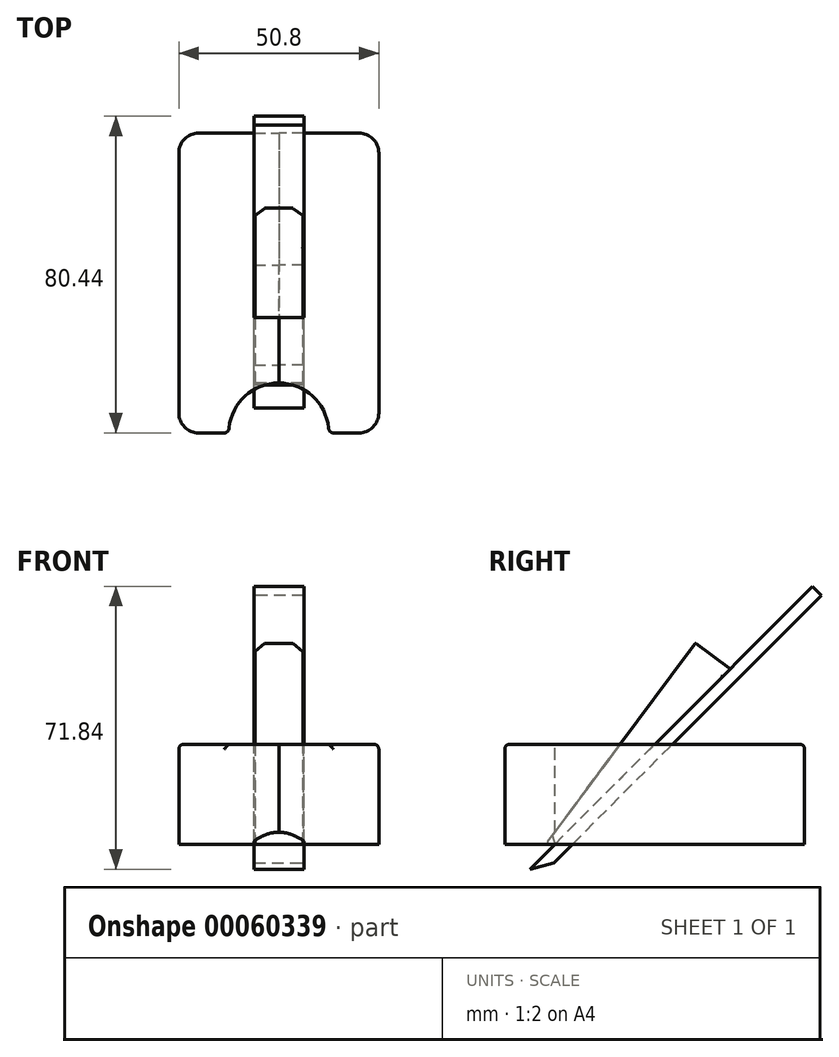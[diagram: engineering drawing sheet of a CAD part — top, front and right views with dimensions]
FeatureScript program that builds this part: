
annotation { "Feature Type Name" : "Feature", "Feature Type Description" : "" }
export const myFeature = defineFeature(function(context is Context, id is Id, definition is map)
    precondition{}
    {
        {
            var Q0;
            Q0=qCreatedBy(makeId("Right.planeOp"),FACE);
            var sketch = newSketch(context, id + "F0", { "sketchPlane" : qUnion([Q0])});
            skLineSegment(sketch, "E0.bottom", {"start": v(38.1, 0) * mm, "end": v(-38.1, 0) * mm});
            skLineSegment(sketch, "E0.top", {"start": v(38.1, 25.4) * mm, "end": v(-38.1, 25.4) * mm});
            skLineSegment(sketch, "E0.left", {"start": v(38.1, 0) * mm, "end": v(38.1, 25.4) * mm});
            skLineSegment(sketch, "E0.right", {"start": v(-38.1, 0) * mm, "end": v(-38.1, 25.4) * mm});
            skSolve(sketch);
        }
        {
            var Q0;
            Q0=qSketchRegion(id+"F0",true);
            extrude(context, id + "F1", {"entities" : qUnion([Q0]), "depth" : 25.4 * mm});
        }
        {
            var Q0;
            Q0=qCreatedBy(makeId("Right.planeOp"),FACE);
            var sketch = newSketch(context, id + "F2", { "sketchPlane" : qUnion([Q0])});
            skLineSegment(sketch, "E1", {"start": v(-29.5, -8.6) * mm, "end": v(42.34, 63.25) * mm});
            skLineSegment(sketch, "E2", {"start": v(40.1, 65.5) * mm, "end": v(42.34, 63.25) * mm});
            skLineSegment(sketch, "E3", {"start": v(-31.75, -6.35) * mm, "end": v(-29.5, -8.6) * mm});
            skLineSegment(sketch, "E4", {"start": v(19.15, 44.55) * mm, "end": v(10.32, 51.1) * mm});
            skLineSegment(sketch, "E5", {"start": v(10.32, 51.1) * mm, "end": v(-26, 2.23) * mm});
            skLineSegment(sketch, "E6", {"start": v(-26, 2.23) * mm, "end": v(-25.4, 0) * mm});
            skLineSegment(sketch, "E7", {"start": v(0, 0) * mm, "end": v(72.47, 0) * mm, "construction": true});
            skLineSegment(sketch, "E8", {"start": v(-25.4, 0) * mm, "end": v(19.15, 44.55) * mm});
            skLineSegment(sketch, "E9", {"start": v(40.1, 65.5) * mm, "end": v(-31.75, -6.35) * mm});
            skSolve(sketch);
        }
        {
            var Q0;
            Q0=qCreatedBy(makeId("Right.planeOp"),FACE);
            var sketch = newSketch(context, id + "F3", { "sketchPlane" : qUnion([Q0])});
            skLineSegment(sketch, "E10", {"start": v(-20.9, 0) * mm, "end": v(4.5, 25.4) * mm});
            skLineSegment(sketch, "E11", {"start": v(-27.66, 0) * mm, "end": v(-20.9, 0) * mm});
            skLineSegment(sketch, "E12", {"start": v(-27.66, 0) * mm, "end": v(-8.78, 25.4) * mm});
            skLineSegment(sketch, "E13", {"start": v(4.5, 25.4) * mm, "end": v(-8.78, 25.4) * mm});
            skSolve(sketch);
        }
        {
            var Q0;
            Q0=qSketchRegion(id+"F3",true);
            extrude(context, id + "F4", {"entities" : qUnion([Q0]), "operationType" : NewBodyOperationType.REMOVE, "depth" : 6.35 * mm});
        }
        {
            var Q0;
            Q0=makeQuery(id+"F1.opExtrude","SWEPT_FACE",FACE,{"disambiguationData":[OSD([sQuery(id+"F0.wireOp",EDGE,"E0.top")])]});
            var sketch = newSketch(context, id + "F5", { "sketchPlane" : qUnion([Q0])});
            skCircle(sketch, "E14", {"center": v(0, -38.1) * mm, "radius": 12.7 * mm});
            skSolve(sketch);
        }
        {
            var Q0;
            {var subQ0=sQuery(id+"F5.wireOp",EDGE,"E14");var subQ1=sQuery(id+"F0.wireOp",EDGE,"E0.right");var subQ2=sQuery(id+"F0.wireOp",EDGE,"E0.top");var subQ3=makeQuery(id+"F9.opPattern","COPY",EDGE,{"derivedFrom":makeQuery(id+"F1.opExtrude","SWEPT_EDGE",EDGE,{"disambiguationData":[OSD([subQ2,subQ1])]}),"instanceName":"1"});var subQ4=makeQuery(id+"F5.imprint","INTERSECT",VERTEX,{"derivedFrom":[subQ3,subQ0]});Q0=makeQuery(id+"F5.imprint","IMPRINT",FACE,{"disambiguationData":[TD([[makeQuery(id+"F5.imprint","IMPRINT",EDGE,{"disambiguationData":[TD([[subQ4,-1.0]])],"derivedFrom":subQ0}),1.0]])]});}
            extrude(context, id + "F6", {"entities" : qUnion([Q0]), "operationType" : NewBodyOperationType.REMOVE, "endBound" : BoundingType.THROUGH_ALL, "oppositeDirection" : true, "depth" : 25.4 * mm});
        }
        {
            var Q0;
            Q0=makeQuery(id+"F1.opExtrude","CAP_EDGE",EDGE,{"disambiguationData":[OSD([sQuery(id+"F0.wireOp",EDGE,"E0.right")])],"isStart":false});
            var Q1;
            Q1=makeQuery(id+"F1.opExtrude","CAP_EDGE",EDGE,{"disambiguationData":[OSD([sQuery(id+"F0.wireOp",EDGE,"E0.left")])],"isStart":false});
            fillet(context, id + "F7", {"entities" : qUnion([Q0, Q1]), "radius" : 5.08 * mm, "tangentPropagation" : true, "allowEdgeOverflow" : false});
        }
        {
            var Q0;
            Q0=makeQuery(id+"F1.opExtrude","CAP_EDGE",EDGE,{"disambiguationData":[OSD([sQuery(id+"F0.wireOp",EDGE,"E0.top")])],"isStart":false});
            var Q1;
            Q1=makeQuery(id+"F6.boolean.opBoolean","COPY",EDGE,{"derivedFrom":makeQuery(id+"F6.opExtrude","CAP_EDGE",EDGE,{"disambiguationData":[OSD([sQuery(id+"F5.wireOp",EDGE,"E14")])],"isStart":true})});
            var Q2;
            Q2=makeQuery(id+"F6.boolean.opBoolean","INTERSECT",EDGE,{"derivedFrom":[makeQuery(id+"F1.opExtrude","SWEPT_FACE",FACE,{"disambiguationData":[OSD([sQuery(id+"F0.wireOp",EDGE,"E0.right")])]}),makeQuery(id+"F6.opExtrude","SWEPT_FACE",FACE,{"disambiguationData":[OSD([sQuery(id+"F5.wireOp",EDGE,"E14")])]})]});
            fillet(context, id + "F8", {"entities" : qUnion([Q0, Q1, Q2]), "radius" : 1.27 * mm, "tangentPropagation" : true, "allowEdgeOverflow" : false});
        }
        {
            var Q0;
            Q0=makeQuery(id+"F1.opExtrude","SWEPT_BODY",BODY,{"disambiguationData":[OSD([sQuery(id+"F0.wireOp",EDGE,"E0.bottom"),sQuery(id+"F0.wireOp",EDGE,"E0.top"),sQuery(id+"F0.wireOp",EDGE,"E0.left"),sQuery(id+"F0.wireOp",EDGE,"E0.right")])]});
            var Q1;
            Q1=qCreatedBy(makeId("Right.planeOp"),FACE);
            mirror(context, id + "F9", {"entities" : qUnion([Q0]), "mirrorPlane" : qUnion([Q1])});
        }
        {
            var Q0;
            Q0=qCreatedBy(makeId("Right.planeOp"),FACE);
            var sketch = newSketch(context, id + "F10", { "sketchPlane" : qUnion([Q0])});
            skLineSegment(sketch, "E15.0", {"start": v(10.32, 51.1) * mm, "end": v(-26, 2.23) * mm});
            skLineSegment(sketch, "E16.0", {"start": v(-25.4, 0) * mm, "end": v(19.15, 44.55) * mm});
            skLineSegment(sketch, "E17.0", {"start": v(-26, 2.23) * mm, "end": v(-25.4, 0) * mm});
            skLineSegment(sketch, "E18.0", {"start": v(19.15, 44.55) * mm, "end": v(10.32, 51.1) * mm});
            skSolve(sketch);
        }
        {
            var Q0;
            Q0=qSketchRegion(id+"F10",true);
            extrude(context, id + "F11", {"entities" : qUnion([Q0]), "endBound" : BoundingType.SYMMETRIC, "depth" : 12.2 * mm});
        }
        {
            var Q0;
            Q0=qCreatedBy(makeId("Right.planeOp"),FACE);
            var sketch = newSketch(context, id + "F12", { "sketchPlane" : qUnion([Q0])});
            skLineSegment(sketch, "E19.0", {"start": v(-31.75, -6.35) * mm, "end": v(-29.5, -8.6) * mm});
            skLineSegment(sketch, "E20.0", {"start": v(-31.75, -6.35) * mm, "end": v(40.1, 65.5) * mm});
            skLineSegment(sketch, "E21.0", {"start": v(-29.5, -8.6) * mm, "end": v(42.34, 63.25) * mm});
            skLineSegment(sketch, "E22.0", {"start": v(40.1, 65.5) * mm, "end": v(42.34, 63.25) * mm});
            skSolve(sketch);
        }
        {
            var Q0;
            Q0=makeQuery(id+"F11.opExtrude","CAP_EDGE",EDGE,{"disambiguationData":[OSD([sQuery(id+"F10.wireOp",EDGE,"E18.0")])],"isStart":true});
            var Q1;
            Q1=makeQuery(id+"F11.opExtrude","CAP_EDGE",EDGE,{"disambiguationData":[OSD([sQuery(id+"F10.wireOp",EDGE,"E18.0")])],"isStart":false});
            chamfer(context, id + "F13", {"entities" : qUnion([Q0, Q1]), "width" : 2.54 * mm, "tangentPropagation" : true});
        }
        {
            var Q0;
            Q0=makeQuery(id+"F11.opExtrude","SWEPT_EDGE",EDGE,{"disambiguationData":[OSD([sQuery(id+"F10.wireOp",EDGE,"E15.0"),sQuery(id+"F10.wireOp",EDGE,"E17.0")])]});
            var Q1;
            {var subQ0=sQuery(id+"F10.wireOp",EDGE,"E18.0");Q1=makeQuery(id+"F13.opChamfer","BLEND_EDGE",EDGE,{"blendedFrom":[makeQuery(id+"F11.opExtrude","CAP_EDGE",EDGE,{"disambiguationData":[OSD([subQ0])],"isStart":false}),makeQuery(id+"F11.opExtrude","SWEPT_FACE",FACE,{"disambiguationData":[OSD([subQ0])]})],"blendedInto":[makeQuery(id+"F11.opExtrude","SWEPT_FACE",FACE,{"disambiguationData":[OSD([subQ0])]})]});}
            var Q2;
            {var subQ0=sQuery(id+"F10.wireOp",EDGE,"E18.0");Q2=makeQuery(id+"F13.opChamfer","BLEND_EDGE",EDGE,{"blendedFrom":[makeQuery(id+"F11.opExtrude","CAP_EDGE",EDGE,{"disambiguationData":[OSD([subQ0])],"isStart":false}),makeQuery(id+"F11.opExtrude","CAP_FACE",FACE,{"disambiguationData":[OSD([sQuery(id+"F10.wireOp",EDGE,"E15.0"),sQuery(id+"F10.wireOp",EDGE,"E16.0"),sQuery(id+"F10.wireOp",EDGE,"E17.0"),subQ0])],"isStart":false})],"blendedInto":[makeQuery(id+"F11.opExtrude","CAP_FACE",FACE,{"disambiguationData":[OSD([sQuery(id+"F10.wireOp",EDGE,"E15.0"),sQuery(id+"F10.wireOp",EDGE,"E16.0"),sQuery(id+"F10.wireOp",EDGE,"E17.0"),subQ0])],"isStart":false})]});}
            var Q3;
            {var subQ0=sQuery(id+"F10.wireOp",EDGE,"E18.0");Q3=makeQuery(id+"F13.opChamfer","BLEND_EDGE",EDGE,{"blendedFrom":[makeQuery(id+"F11.opExtrude","CAP_EDGE",EDGE,{"disambiguationData":[OSD([subQ0])],"isStart":true}),makeQuery(id+"F11.opExtrude","SWEPT_FACE",FACE,{"disambiguationData":[OSD([subQ0])]})],"blendedInto":[makeQuery(id+"F11.opExtrude","SWEPT_FACE",FACE,{"disambiguationData":[OSD([subQ0])]})]});}
            var Q4;
            {var subQ0=sQuery(id+"F10.wireOp",EDGE,"E18.0");Q4=makeQuery(id+"F13.opChamfer","BLEND_EDGE",EDGE,{"blendedFrom":[makeQuery(id+"F11.opExtrude","CAP_EDGE",EDGE,{"disambiguationData":[OSD([subQ0])],"isStart":true}),makeQuery(id+"F11.opExtrude","CAP_FACE",FACE,{"disambiguationData":[OSD([sQuery(id+"F10.wireOp",EDGE,"E15.0"),sQuery(id+"F10.wireOp",EDGE,"E16.0"),sQuery(id+"F10.wireOp",EDGE,"E17.0"),subQ0])],"isStart":true})],"blendedInto":[makeQuery(id+"F11.opExtrude","CAP_FACE",FACE,{"disambiguationData":[OSD([sQuery(id+"F10.wireOp",EDGE,"E15.0"),sQuery(id+"F10.wireOp",EDGE,"E16.0"),sQuery(id+"F10.wireOp",EDGE,"E17.0"),subQ0])],"isStart":true})]});}
            var Q5;
            Q5=makeQuery(id+"F11.opExtrude","SWEPT_EDGE",EDGE,{"disambiguationData":[OSD([sQuery(id+"F10.wireOp",EDGE,"E15.0"),sQuery(id+"F10.wireOp",EDGE,"E18.0")])]});
            var Q6;
            Q6=makeQuery(id+"F13.opChamfer","BLEND_EDGE",EDGE,{"blendedFrom":[makeQuery(id+"F11.opExtrude","CAP_EDGE",EDGE,{"disambiguationData":[OSD([sQuery(id+"F10.wireOp",EDGE,"E18.0")])],"isStart":true}),makeQuery(id+"F11.opExtrude","SWEPT_FACE",FACE,{"disambiguationData":[OSD([sQuery(id+"F10.wireOp",EDGE,"E15.0")])]})],"blendedInto":[makeQuery(id+"F11.opExtrude","SWEPT_FACE",FACE,{"disambiguationData":[OSD([sQuery(id+"F10.wireOp",EDGE,"E15.0")])]})]});
            var Q7;
            Q7=makeQuery(id+"F13.opChamfer","BLEND_EDGE",EDGE,{"blendedFrom":[makeQuery(id+"F11.opExtrude","CAP_EDGE",EDGE,{"disambiguationData":[OSD([sQuery(id+"F10.wireOp",EDGE,"E18.0")])],"isStart":false}),makeQuery(id+"F11.opExtrude","SWEPT_FACE",FACE,{"disambiguationData":[OSD([sQuery(id+"F10.wireOp",EDGE,"E15.0")])]})],"blendedInto":[makeQuery(id+"F11.opExtrude","SWEPT_FACE",FACE,{"disambiguationData":[OSD([sQuery(id+"F10.wireOp",EDGE,"E15.0")])]})]});
            var Q8;
            Q8=makeQuery(id+"F13.opChamfer","BLEND_EDGE",EDGE,{"blendedFrom":[makeQuery(id+"F11.opExtrude","CAP_EDGE",EDGE,{"disambiguationData":[OSD([sQuery(id+"F10.wireOp",EDGE,"E18.0")])],"isStart":true}),makeQuery(id+"F11.opExtrude","SWEPT_FACE",FACE,{"disambiguationData":[OSD([sQuery(id+"F10.wireOp",EDGE,"E16.0")])]})],"blendedInto":[makeQuery(id+"F11.opExtrude","SWEPT_FACE",FACE,{"disambiguationData":[OSD([sQuery(id+"F10.wireOp",EDGE,"E16.0")])]})]});
            var Q9;
            Q9=makeQuery(id+"F13.opChamfer","BLEND_EDGE",EDGE,{"blendedFrom":[makeQuery(id+"F11.opExtrude","CAP_EDGE",EDGE,{"disambiguationData":[OSD([sQuery(id+"F10.wireOp",EDGE,"E18.0")])],"isStart":false}),makeQuery(id+"F11.opExtrude","SWEPT_FACE",FACE,{"disambiguationData":[OSD([sQuery(id+"F10.wireOp",EDGE,"E16.0")])]})],"blendedInto":[makeQuery(id+"F11.opExtrude","SWEPT_FACE",FACE,{"disambiguationData":[OSD([sQuery(id+"F10.wireOp",EDGE,"E16.0")])]})]});
            var Q10;
            Q10=makeQuery(id+"F11.opExtrude","SWEPT_EDGE",EDGE,{"disambiguationData":[OSD([sQuery(id+"F10.wireOp",EDGE,"E16.0"),sQuery(id+"F10.wireOp",EDGE,"E18.0")])]});
            fillet(context, id + "F14", {"entities" : qUnion([Q0, Q1, Q2, Q3, Q4, Q5, Q6, Q7, Q8, Q9, Q10]), "radius" : 0.25 * mm, "tangentPropagation" : true, "allowEdgeOverflow" : false});
        }
        {
            var Q0;
            Q0=qSketchRegion(id+"F12",true);
            extrude(context, id + "F15", {"entities" : qUnion([Q0]), "endBound" : BoundingType.SYMMETRIC, "depth" : 12.7 * mm});
        }
        {
            var Q0;
            Q0=makeQuery(id+"F15.opExtrude","CAP_FACE",FACE,{"disambiguationData":[OSD([sQuery(id+"F12.wireOp",EDGE,"E19.0"),sQuery(id+"F12.wireOp",EDGE,"E20.0"),sQuery(id+"F12.wireOp",EDGE,"E21.0"),sQuery(id+"F12.wireOp",EDGE,"E22.0")])],"isStart":false});
            var sketch = newSketch(context, id + "F16", { "sketchPlane" : qUnion([Q0])});
            skLineSegment(sketch, "E23.0", {"start": v(-31.75, -6.35) * mm, "end": v(-29.5, -8.6) * mm});
            skLineSegment(sketch, "E23.1", {"start": v(-29.5, -8.6) * mm, "end": v(-25.62, -4.7) * mm});
            skLineSegment(sketch, "E24", {"start": v(-31.75, -6.35) * mm, "end": v(-25.62, -4.7) * mm});
            skSolve(sketch);
        }
        {
            var Q0;
            Q0=makeQuery(id+"F16.imprint","IMPRINT",FACE,{"disambiguationData":[TD([[makeQuery(id+"F16.imprint","IMPRINT",EDGE,{"derivedFrom":sQuery(id+"F16.wireOp",EDGE,"E23.0")}),1.0]])]});
            extrude(context, id + "F17", {"entities" : qUnion([Q0]), "operationType" : NewBodyOperationType.REMOVE, "endBound" : BoundingType.THROUGH_ALL, "oppositeDirection" : true, "depth" : 25.4 * mm});
        }
    });
